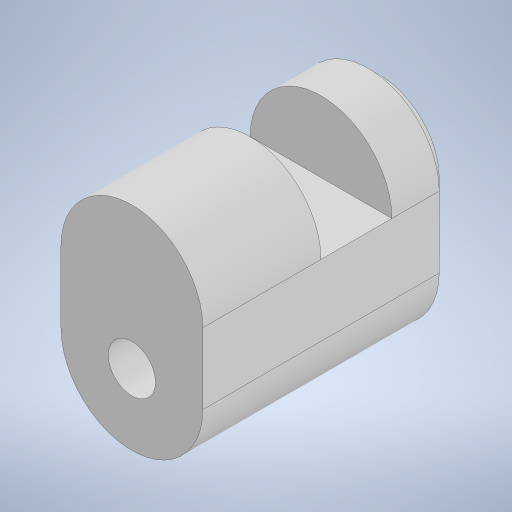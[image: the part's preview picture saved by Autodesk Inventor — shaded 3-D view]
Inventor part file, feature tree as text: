
AUTODESK INVENTOR PART (.ipt)
format: ipt  version: 2024.1 (Build 281209000, 209)  size: 236,544 bytes
history: native  units: mm
features: extrude x4, sketch x4, projected_geometry x3, chamfer x2
ambient origin geometry x8: Origin, YZ Plane, XZ Plane, XY Plane, X Axis, Y Axis, Z Axis, Center Point
bodies: Solid1 (feature_tree)
feature tree (13):
  extrude  "Extrusion1"  Depth=12.0mm
  extrude  "Extrusion2"  Depth=6.0mm
  extrude  "Extrusion3"  Depth=10.0mm TaperAngle=0.0deg
  extrude  "Extrusion4"  Depth=2.0mm TaperAngle=0.0deg
  chamfer  "Chamfer1"  Distance=2.0mm Angle=45.0deg
  chamfer  "Chamfer2"  Distance=2.0mm Angle=45.0deg
  sketch  "Sketch2"  dims[d0=12.0mm d1=4.0mm]
  sketch  "Sketch3"  dims[d2=21.0mm d3=0.0mm d4=6.0mm]
  projected_geometry  "Projected Loop1"
  sketch  "Sketch4"  dims[d5=6.0mm d6=10.0mm d7=0.0mm]
  projected_geometry  "Projected Loop2"
  sketch  "Sketch5"  dims[d8=5.0mm d9=0.0mm d10=6.4mm d11=0.0mm d12=3.0mm d13=2.0mm d14=45.0deg d15=1.0mm d16=2.0mm d17=45.0deg]
  projected_geometry  "Projected Loop3"
